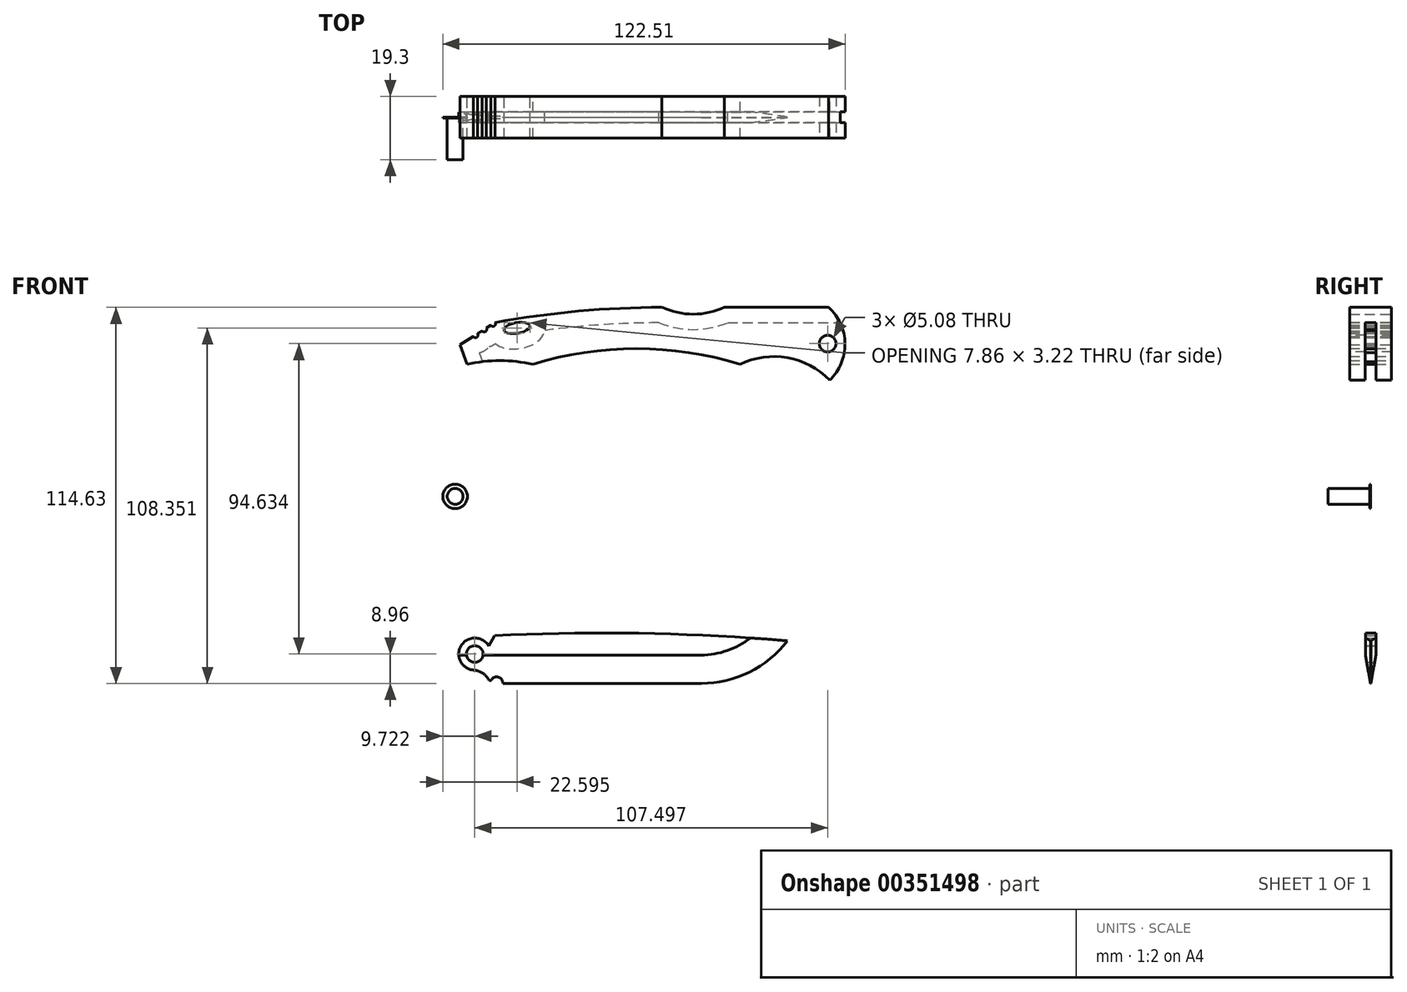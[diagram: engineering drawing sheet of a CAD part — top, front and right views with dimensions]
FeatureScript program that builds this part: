
annotation { "Feature Type Name" : "Feature", "Feature Type Description" : "" }
export const myFeature = defineFeature(function(context is Context, id is Id, definition is map)
    precondition{}
    {
        {
            var Q0;
            Q0=qCreatedBy(makeId("Front.planeOp"),FACE);
            var sketch = newSketch(context, id + "F0", { "sketchPlane" : qUnion([Q0])});
            skLineSegment(sketch, "E0", {"start": v(12.22, 35.98) * mm, "end": v(43.97, 35.98) * mm});
            skArc(sketch, "E1", {"start": v(-6.83, 35.98) * mm, "mid": v(-32.34, 34.82) * mm, "end": v(-57.63, 31.34) * mm});
            skPoint(sketch, "E2.orphan", {"position": v(-57.63, 35.98) * mm});
            skLineSegment(sketch, "E3", {"start": v(-58.98, 30.5) * mm, "end": v(-60.33, 29.65) * mm});
            skLineSegment(sketch, "E4", {"start": v(-68.4, 24.6) * mm, "end": v(-66.26, 18.63) * mm});
            skArc(sketch, "E5", {"start": v(-46.16, 18.63) * mm, "mid": v(-56.21, 19.75) * mm, "end": v(-66.26, 18.63) * mm});
            skArc(sketch, "E6", {"start": v(16.92, 18.63) * mm, "mid": v(-14.62, 23.42) * mm, "end": v(-46.16, 18.63) * mm});
            skArc(sketch, "E7", {"start": v(44.27, 13.78) * mm, "mid": v(31.37, 20.62) * mm, "end": v(16.92, 18.63) * mm});
            skArc(sketch, "E8", {"start": v(44.27, 13.78) * mm, "mid": v(48.92, 24.94) * mm, "end": v(43.97, 35.98) * mm});
            skLineSegment(sketch, "E9", {"start": v(-61.67, 28.81) * mm, "end": v(-63.02, 27.97) * mm});
            skLineSegment(sketch, "E10", {"start": v(-64.36, 27.13) * mm, "end": v(-65.71, 26.29) * mm});
            skArc(sketch, "E11", {"start": v(-58.98, 30.5) * mm, "mid": v(-57.9, 30.28) * mm, "end": v(-57.63, 31.34) * mm});
            skArc(sketch, "E12", {"start": v(-61.67, 28.81) * mm, "mid": v(-60.6, 28.58) * mm, "end": v(-60.33, 29.65) * mm});
            skArc(sketch, "E13", {"start": v(-64.36, 27.13) * mm, "mid": v(-63.26, 26.86) * mm, "end": v(-63.02, 27.97) * mm});
            skLineSegment(sketch, "E14.trimOffspring", {"start": v(-64.36, 27.13) * mm, "end": v(-68.4, 24.6) * mm});
            skEllipse(sketch, "E15", {"center": v(-51, 29.7) * mm, "majorRadius": 3.99 * mm, "minorRadius": 1.63 * mm, "majorAxis": v(0.99, 0.17)});
            skArc(sketch, "E16", {"start": v(-6.83, 35.98) * mm, "mid": v(2.7, 33.91) * mm, "end": v(12.22, 35.98) * mm});
            skArc(sketch, "E17", {"start": v(-59.66, -67.2) * mm, "mid": v(-68.05, -67.15) * mm, "end": v(-64.13, -74.57) * mm});
            skLineSegment(sketch, "E18", {"start": v(-59.66, -67.2) * mm, "end": v(-57.78, -64.08) * mm});
            skArc(sketch, "E19", {"start": v(31.38, -65.64) * mm, "mid": v(-13.17, -63.35) * mm, "end": v(-57.78, -64.08) * mm});
            skPoint(sketch, "E19.startSnap0", {"position": v(-58.72, -65.64) * mm});
            skArc(sketch, "E20", {"start": v(5.11, -78.65) * mm, "mid": v(19.75, -75.18) * mm, "end": v(31.38, -65.64) * mm});
            skLineSegment(sketch, "E21", {"start": v(5.11, -78.65) * mm, "end": v(-55.28, -78.65) * mm});
            skArc(sketch, "E22", {"start": v(-55.28, -78.65) * mm, "mid": v(-56.8, -76.7) * mm, "end": v(-59.01, -77.8) * mm});
            skArc(sketch, "E23", {"start": v(-59.5, -77.8) * mm, "mid": v(-61.42, -75.52) * mm, "end": v(-64.24, -74.57) * mm});
            skLineSegment(sketch, "E24", {"start": v(-59.5, -77.8) * mm, "end": v(-59.01, -77.8) * mm});
            skPoint(sketch, "E25.orphan", {"position": v(-59.18, -78.65) * mm});
            skCircle(sketch, "E26", {"center": v(-63.87, -69.69) * mm, "radius": 2.54 * mm});
            skPoint(sketch, "E27.end.orphan", {"position": v(-87.05, -44.14) * mm});
            skPoint(sketch, "E27.start.orphan", {"position": v(-87.05, -94.94) * mm});
            skSolve(sketch);
        }
        {
            var Q0;
            Q0=makeQuery(id+"F0.imprint","IMPRINT",FACE,{"disambiguationData":[TD([[makeQuery(id+"F0.imprint","IMPRINT",EDGE,{"derivedFrom":sQuery(id+"F0.wireOp",EDGE,"E0")}),-1.0]])]});
            extrude(context, id + "F1", {"entities" : qUnion([Q0]), "endBound" : BoundingType.SYMMETRIC, "depth" : 12.7 * mm});
        }
        {
            var Q0;
            {var subQ0=sQuery(id+"F0.wireOp",EDGE,"E18");Q0=makeQuery(id+"F0.imprint","IMPRINT",FACE,{"disambiguationData":[TD([[makeQuery(id+"F0.imprint","IMPRINT",EDGE,{"derivedFrom":subQ0}),-1.0]])]});}
            extrude(context, id + "F2", {"entities" : qUnion([Q0]), "endBound" : BoundingType.SYMMETRIC, "depth" : 3.17 * mm});
        }
        {
            var Q0;
            Q0=makeQuery(id+"F1.opExtrude","SWEPT_FACE",FACE,{"disambiguationData":[OSD([sQuery(id+"F0.wireOp",EDGE,"E7")])]});
            var Q1;
            Q1=makeQuery(id+"F1.opExtrude","SWEPT_FACE",FACE,{"disambiguationData":[OSD([sQuery(id+"F0.wireOp",EDGE,"E6")])]});
            var Q2;
            Q2=makeQuery(id+"F1.opExtrude","SWEPT_FACE",FACE,{"disambiguationData":[OSD([sQuery(id+"F0.wireOp",EDGE,"E5")])]});
            var Q3;
            Q3=makeQuery(id+"F1.opExtrude","SWEPT_FACE",FACE,{"disambiguationData":[OSD([sQuery(id+"F0.wireOp",EDGE,"E8")])]});
            shell(context, id + "F3", {"entities" : qUnion([Q0, Q1, Q2, Q3]), "thickness" : 4.7 * mm});
        }
        {
            var Q0;
            Q0=qCreatedBy(makeId("Front.planeOp"),FACE);
            var sketch = newSketch(context, id + "F4", { "sketchPlane" : qUnion([Q0])});
            skCircle(sketch, "E28", {"center": v(-69.85, -21.64) * mm, "radius": 3.73 * mm});
            skSolve(sketch);
        }
        {
            var Q0;
            Q0=makeQuery(id+"F4.imprint","IMPRINT",FACE,{"disambiguationData":[TD([[makeQuery(id+"F4.imprint","IMPRINT",EDGE,{"derivedFrom":sQuery(id+"F4.wireOp",EDGE,"E28")}),1.0]])]});
            extrude(context, id + "F5", {"entities" : qUnion([Q0]), "depth" : 0.25 * mm});
        }
        {
            var Q0;
            Q0=makeQuery(id+"F5.opExtrude","CAP_FACE",FACE,{"disambiguationData":[OSD([sQuery(id+"F4.wireOp",EDGE,"E28")])],"isStart":false});
            var sketch = newSketch(context, id + "F6", { "sketchPlane" : qUnion([Q0])});
            skCircle(sketch, "E29", {"center": v(-69.85, -21.64) * mm, "radius": 2.41 * mm});
            skSolve(sketch);
        }
        {
            var Q0;
            Q0=makeQuery(id+"F6.imprint","IMPRINT",FACE,{"disambiguationData":[TD([[makeQuery(id+"F6.imprint","IMPRINT",EDGE,{"derivedFrom":sQuery(id+"F6.wireOp",EDGE,"E29")}),1.0]])]});
            extrude(context, id + "F7", {"entities" : qUnion([Q0]), "operationType" : NewBodyOperationType.ADD, "depth" : 12.7 * mm});
        }
        {
            var Q0;
            Q0=makeQuery(id+"F2.opExtrude","CAP_EDGE",EDGE,{"disambiguationData":[OSD([sQuery(id+"F0.wireOp",EDGE,"E21")])],"isStart":false});
            var Q1;
            Q1=makeQuery(id+"F2.opExtrude","CAP_EDGE",EDGE,{"disambiguationData":[OSD([sQuery(id+"F0.wireOp",EDGE,"E20")])],"isStart":false});
            chamfer(context, id + "F8", {"entities" : qUnion([Q0, Q1]), "chamferType" : ChamferType.OFFSET_ANGLE, "width" : 1.52 * mm, "oppositeDirection" : false, "angle" : 80 * degree, "tangentPropagation" : true});
        }
        {
            var Q0;
            Q0=makeQuery(id+"F2.opExtrude","CAP_EDGE",EDGE,{"disambiguationData":[OSD([sQuery(id+"F0.wireOp",EDGE,"E20")])],"isStart":true});
            var Q1;
            Q1=makeQuery(id+"F2.opExtrude","CAP_EDGE",EDGE,{"disambiguationData":[OSD([sQuery(id+"F0.wireOp",EDGE,"E21")])],"isStart":true});
            chamfer(context, id + "F9", {"entities" : qUnion([Q0, Q1]), "chamferType" : ChamferType.OFFSET_ANGLE, "width" : 1.52 * mm, "oppositeDirection" : false, "angle" : 80 * degree, "tangentPropagation" : true});
        }
        {
            var Q0;
            Q0=makeQuery(id+"F1.opExtrude","CAP_FACE",FACE,{"disambiguationData":[OSD([sQuery(id+"F0.wireOp",EDGE,"E0"),sQuery(id+"F0.wireOp",EDGE,"E1"),sQuery(id+"F0.wireOp",EDGE,"E4"),sQuery(id+"F0.wireOp",EDGE,"E5"),sQuery(id+"F0.wireOp",EDGE,"E6"),sQuery(id+"F0.wireOp",EDGE,"E7"),sQuery(id+"F0.wireOp",EDGE,"E8"),sQuery(id+"F0.wireOp",EDGE,"E3"),sQuery(id+"F0.wireOp",EDGE,"E11"),sQuery(id+"F0.wireOp",EDGE,"E12"),sQuery(id+"F0.wireOp",EDGE,"E13"),sQuery(id+"F0.wireOp",EDGE,"E9"),sQuery(id+"F0.wireOp",EDGE,"E14.trimOffspring"),sQuery(id+"F0.wireOp",EDGE,"E15"),sQuery(id+"F0.wireOp",EDGE,"E16")])],"isStart":false});
            var sketch = newSketch(context, id + "F10", { "sketchPlane" : qUnion([Q0])});
            skCircle(sketch, "E30", {"center": v(43.63, 24.94) * mm, "radius": 2.54 * mm});
            skPoint(sketch, "E30.centerSnap0", {"position": v(48.92, 24.94) * mm});
            skSolve(sketch);
        }
        {
            var Q0;
            Q0=makeQuery(id+"F10.imprint","IMPRINT",FACE,{"disambiguationData":[TD([[makeQuery(id+"F10.imprint","IMPRINT",EDGE,{"derivedFrom":sQuery(id+"F10.wireOp",EDGE,"E30")}),1.0]])]});
            extrude(context, id + "F11", {"entities" : qUnion([Q0]), "operationType" : NewBodyOperationType.REMOVE, "oppositeDirection" : true, "depth" : 25.4 * mm});
        }
    });
